annotation { "Feature Type Name" : "Feature", "Feature Type Description" : "" }
export const myFeature = defineFeature(function(context is Context, id is Id, definition is map)
    precondition{}
    {
        {
            var Q0;
            Q0=qCreatedBy(makeId("Front.planeOp"),FACE);
            var sketch = newSketch(context, id + "F0", { "sketchPlane" : qUnion([Q0])});
            skText(sketch, "E0", { "text": "NOW SPINNING", "fontName": "NotoSans-Bold.ttf"});
            const initialGuessF0  = {"E0": [-0.07131, 0, 1, 0, 0.01612]};
            skSetInitialGuess(sketch, initialGuessF0);
            skSolve(sketch);
        }
        {
            var Q0;
            Q0 = qSketchRegion(id + "F0", true);
            extrude(context, id + "F1", {"entities" : qUnion([Q0]), "depth" : 38.1 * mm, "offsetDistance" : 25.4 * mm});
        }
        {
            var Q0;
            Q0=qCreatedBy(makeId("Right.planeOp"),FACE);
            var sketch = newSketch(context, id + "F2", { "sketchPlane" : qUnion([Q0])});
            skLineSegment(sketch, "E1", {"start": v(-31.75, 16.24) * mm, "end": v(-29.07, 13.56) * mm});
            skLineSegment(sketch, "E2", {"start": v(-28.18, 13.19) * mm, "end": v(-9.28, 13.19) * mm});
            skLineSegment(sketch, "E3", {"start": v(-8.18, 13.82) * mm, "end": v(-6.79, 16.24) * mm});
            skArc(sketch, "E4.filletArc", {"start": v(-29.07, 13.56) * mm, "mid": v(-28.66, 13.29) * mm, "end": v(-28.18, 13.19) * mm});
            skPoint(sketch, "E5.visualSharp", {"position": v(-8.55, 13.19) * mm});
            skArc(sketch, "E5.filletArc", {"start": v(-9.28, 13.19) * mm, "mid": v(-8.65, 13.36) * mm, "end": v(-8.18, 13.82) * mm});
            skLineSegment(sketch, "E6", {"start": v(-31.75, 16.24) * mm, "end": v(-6.79, 16.24) * mm});
            skSolve(sketch);
        }
        {
            var Q0;
            Q0=makeQuery(id+"F2.imprint","IMPRINT",FACE,{"disambiguationData":[TD([[makeQuery(id+"F2.imprint","IMPRINT",EDGE,{"derivedFrom":sQuery(id+"F2.wireOp",EDGE,"E1")}),1.0]])]});
            extrude(context, id + "F3", {"entities" : qUnion([Q0]), "operationType" : NewBodyOperationType.REMOVE, "endBound" : BoundingType.SYMMETRIC, "depth" : 255.02 * mm, "offsetDistance" : 25.4 * mm});
        }
        {
            var Q0;
            Q0=makeQuery(id+"F1.opExtrude","SWEPT_FACE",FACE,{"disambiguationData":[OSD([sQuery(id+"F0.wireOp",EDGE,"E0.sketch_text.stroke-6")])]});
            var sketch = newSketch(context, id + "F4", { "sketchPlane" : qUnion([Q0])});
            skLineSegment(sketch, "E7.bottom", {"start": v(0, 22.56) * mm, "end": v(-1.27, 22.56) * mm});
            skLineSegment(sketch, "E7.top", {"start": v(-1.27, 0) * mm, "end": v(0, 0) * mm});
            skLineSegment(sketch, "E7.left", {"start": v(-1.27, 22.56) * mm, "end": v(-1.27, 0) * mm});
            skLineSegment(sketch, "E7.right", {"start": v(0, 22.56) * mm, "end": v(0, 0) * mm});
            skLineSegment(sketch, "E8", {"start": v(0, 22.56) * mm, "end": v(2.22, 16.45) * mm});
            skLineSegment(sketch, "E9", {"start": v(2.22, 16.45) * mm, "end": v(2.22, 0) * mm});
            skLineSegment(sketch, "E10", {"start": v(2.22, 0) * mm, "end": v(0, 0) * mm});
            skSolve(sketch);
        }
        {
            var Q0;
            Q0 = qSketchRegion(id + "F4", true);
            var Q1;
            Q1=makeQuery(id+"F1.opExtrude","SWEPT_FACE",FACE,{"disambiguationData":[OSD([sQuery(id+"F0.wireOp",EDGE,"E0.sketch_text.stroke-163")])]});
            extrude(context, id + "F5", {"entities" : qUnion([Q0]), "endBound" : BoundingType.UP_TO_SURFACE, "oppositeDirection" : true, "depth" : 25.4 * mm, "endBoundEntityFace" : qUnion([Q1]), "offsetDistance" : 25.4 * mm});
        }
        {
            var Q0;
            Q0=makeQuery(id+"F5.opExtrude","SWEPT_FACE",FACE,{"disambiguationData":[OSD([sQuery(id+"F4.wireOp",EDGE,"E9")])]});
            var sketch = newSketch(context, id + "F6", { "sketchPlane" : qUnion([Q0])});
            skLineSegment(sketch, "E11", {"start": v(-69.3, 16.21) * mm, "end": v(-56.6, 16.21) * mm});
            skLineSegment(sketch, "E12", {"start": v(-56.6, 16.21) * mm, "end": v(-52.93, 22.56) * mm});
            skLineSegment(sketch, "E13", {"start": v(-52.93, 22.56) * mm, "end": v(-40.23, 22.56) * mm});
            skLineSegment(sketch, "E14", {"start": v(-40.23, 22.56) * mm, "end": v(-36.57, 16.21) * mm});
            skLineSegment(sketch, "E15", {"start": v(-36.57, 16.21) * mm, "end": v(72.3, 16.21) * mm});
            skLineSegment(sketch, "E16", {"start": v(72.3, 16.21) * mm, "end": v(75.97, 22.56) * mm});
            skLineSegment(sketch, "E17", {"start": v(75.97, 22.56) * mm, "end": v(88.67, 22.56) * mm});
            skLineSegment(sketch, "E18", {"start": v(88.67, 22.56) * mm, "end": v(92.34, 16.21) * mm});
            skLineSegment(sketch, "E19", {"start": v(92.31, 16.21) * mm, "end": v(92.34, 16.21) * mm});
            skLineSegment(sketch, "E20", {"start": v(92.34, 16.21) * mm, "end": v(105.04, 16.21) * mm});
            skSolve(sketch);
        }
        {
            var Q0;
            Q0 = qSketchRegion(id + "F6", true);
            var Q1;
            {var subQ0=sQuery(id+"F6.wireOp",EDGE,"E11");Q1=makeQuery(id+"F6.imprint","IMPRINT",FACE,{"disambiguationData":[TD([[makeQuery(id+"F6.imprint","IMPRINT",EDGE,{"derivedFrom":subQ0}),1.0]])]});}
            var Q2;
            {var subQ0=sQuery(id+"F6.wireOp",EDGE,"E14");Q2=makeQuery(id+"F6.imprint","IMPRINT",FACE,{"disambiguationData":[TD([[makeQuery(id+"F6.imprint","IMPRINT",EDGE,{"derivedFrom":subQ0}),1.0]])]});}
            var Q3;
            {var subQ0=sQuery(id+"F6.wireOp",EDGE,"E18");Q3=makeQuery(id+"F6.imprint","IMPRINT",FACE,{"disambiguationData":[TD([[makeQuery(id+"F6.imprint","IMPRINT",EDGE,{"derivedFrom":subQ0}),1.0]])]});}
            extrude(context, id + "F7", {"entities" : qUnion([Q0, Q1, Q2, Q3]), "operationType" : NewBodyOperationType.REMOVE, "oppositeDirection" : true, "depth" : 25.4 * mm, "offsetDistance" : 25.4 * mm});
        }
    });